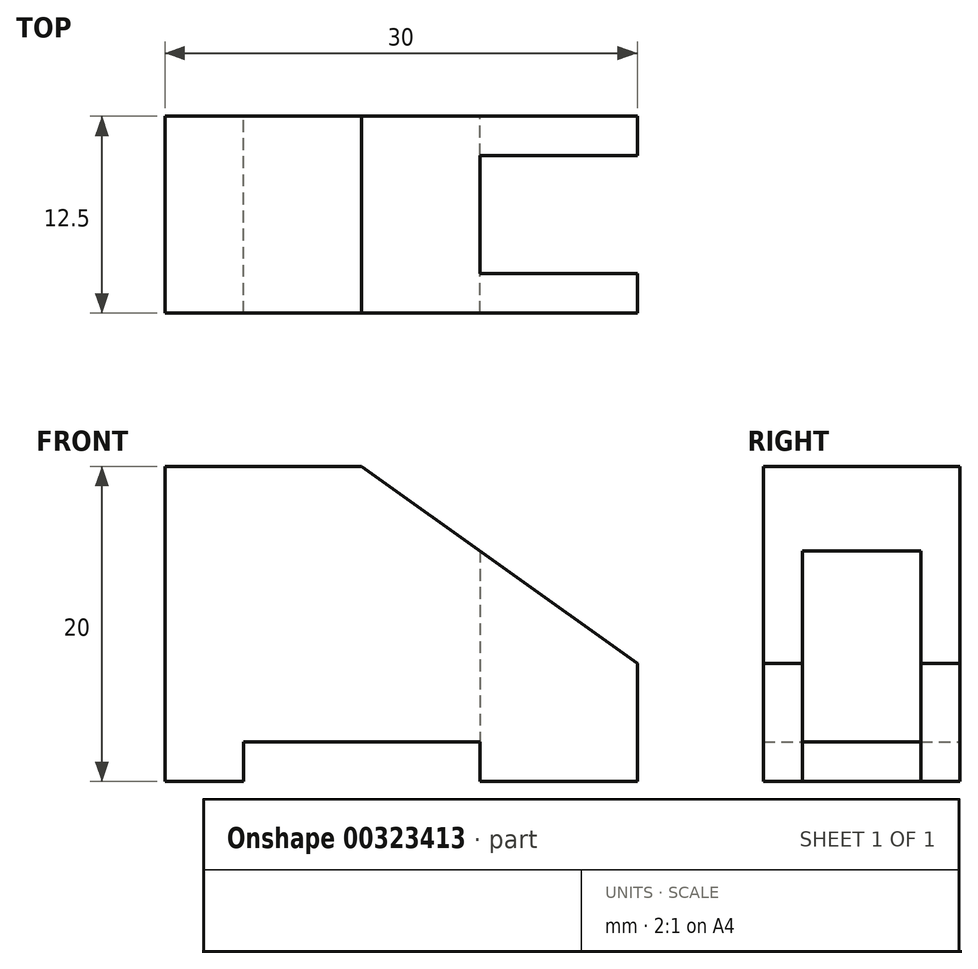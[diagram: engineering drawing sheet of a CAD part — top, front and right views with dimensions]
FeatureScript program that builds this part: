
annotation { "Feature Type Name" : "Feature", "Feature Type Description" : "" }
export const myFeature = defineFeature(function(context is Context, id is Id, definition is map)
    precondition{}
    {
        {
            var Q0;
            Q0=qCreatedBy(makeId("Front.planeOp"),FACE);
            var sketch = newSketch(context, id + "F0", { "sketchPlane" : qUnion([Q0])});
            skLineSegment(sketch, "E0", {"start": v(0, 0) * mm, "end": v(0, 20) * mm});
            skLineSegment(sketch, "E1", {"start": v(0, 20) * mm, "end": v(12.5, 20) * mm});
            skLineSegment(sketch, "E2", {"start": v(12.5, 20) * mm, "end": v(30, 7.5) * mm});
            skLineSegment(sketch, "E3", {"start": v(30, 7.5) * mm, "end": v(30, 0) * mm});
            skLineSegment(sketch, "E4", {"start": v(30, 0) * mm, "end": v(20, 0) * mm});
            skLineSegment(sketch, "E5", {"start": v(20, 0) * mm, "end": v(20, 2.5) * mm});
            skLineSegment(sketch, "E6", {"start": v(20, 2.5) * mm, "end": v(5, 2.5) * mm});
            skLineSegment(sketch, "E7", {"start": v(5, 2.5) * mm, "end": v(5, 0) * mm});
            skLineSegment(sketch, "E8", {"start": v(5, 0) * mm, "end": v(0, 0) * mm});
            skLineSegment(sketch, "E9", {"start": v(20, 2.5) * mm, "end": v(20, 14.64) * mm});
            skSolve(sketch);
        }
        {
            var Q0;
            Q0 = qSketchRegion(id + "F0", true);
            extrude(context, id + "F1", {"entities" : qUnion([Q0]), "depth" : 2.5 * mm});
        }
        {
            var Q0;
            Q0=makeQuery(id+"F0.imprint","IMPRINT",FACE,{"disambiguationData":[TD([[makeQuery(id+"F0.imprint","IMPRINT",EDGE,{"derivedFrom":sQuery(id+"F0.wireOp",EDGE,"E0")}),-1.0]])]});
            extrude(context, id + "F2", {"entities" : qUnion([Q0]), "operationType" : NewBodyOperationType.ADD, "depth" : 10 * mm});
        }
        {
            var Q0;
            Q0=makeQuery(id+"F2.opExtrude","CAP_FACE",FACE,{"disambiguationData":[OSD([sQuery(id+"F0.wireOp",EDGE,"E0"),sQuery(id+"F0.wireOp",EDGE,"E1"),sQuery(id+"F0.wireOp",EDGE,"E2"),sQuery(id+"F0.wireOp",EDGE,"E6"),sQuery(id+"F0.wireOp",EDGE,"E7"),sQuery(id+"F0.wireOp",EDGE,"E8"),sQuery(id+"F0.wireOp",EDGE,"E9")])],"isStart":false});
            var sketch = newSketch(context, id + "F3", { "sketchPlane" : qUnion([Q0])});
            skLineSegment(sketch, "E10.0", {"start": v(20, 14.64) * mm, "end": v(30, 7.5) * mm});
            skLineSegment(sketch, "E11.0", {"start": v(12.5, 20) * mm, "end": v(20, 14.64) * mm});
            skLineSegment(sketch, "E12.0", {"start": v(0, 20) * mm, "end": v(12.5, 20) * mm});
            skLineSegment(sketch, "E13.0", {"start": v(0, 0) * mm, "end": v(0, 20) * mm});
            skLineSegment(sketch, "E14.0", {"start": v(20, 2.5) * mm, "end": v(5, 2.5) * mm});
            skLineSegment(sketch, "E15.0", {"start": v(20, 0) * mm, "end": v(20, 2.5) * mm});
            skLineSegment(sketch, "E16.0", {"start": v(5, 2.5) * mm, "end": v(5, 0) * mm});
            skLineSegment(sketch, "E17.0", {"start": v(5, 0) * mm, "end": v(0, 0) * mm});
            skLineSegment(sketch, "E18.0.0", {"start": v(30, 7.5) * mm, "end": v(20, 14.64) * mm});
            skLineSegment(sketch, "E18.0.1", {"start": v(20, 14.64) * mm, "end": v(20, 2.5) * mm});
            skLineSegment(sketch, "E18.0.2", {"start": v(20, 2.5) * mm, "end": v(20, 0) * mm});
            skLineSegment(sketch, "E18.0.3", {"start": v(20, 0) * mm, "end": v(30, 0) * mm});
            skLineSegment(sketch, "E18.0.4", {"start": v(30, 0) * mm, "end": v(30, 7.5) * mm});
            skSolve(sketch);
        }
        {
            var Q0;
            Q0 = qSketchRegion(id + "F3", true);
            extrude(context, id + "F4", {"entities" : qUnion([Q0]), "operationType" : NewBodyOperationType.ADD, "depth" : 2.5 * mm});
        }
    });
